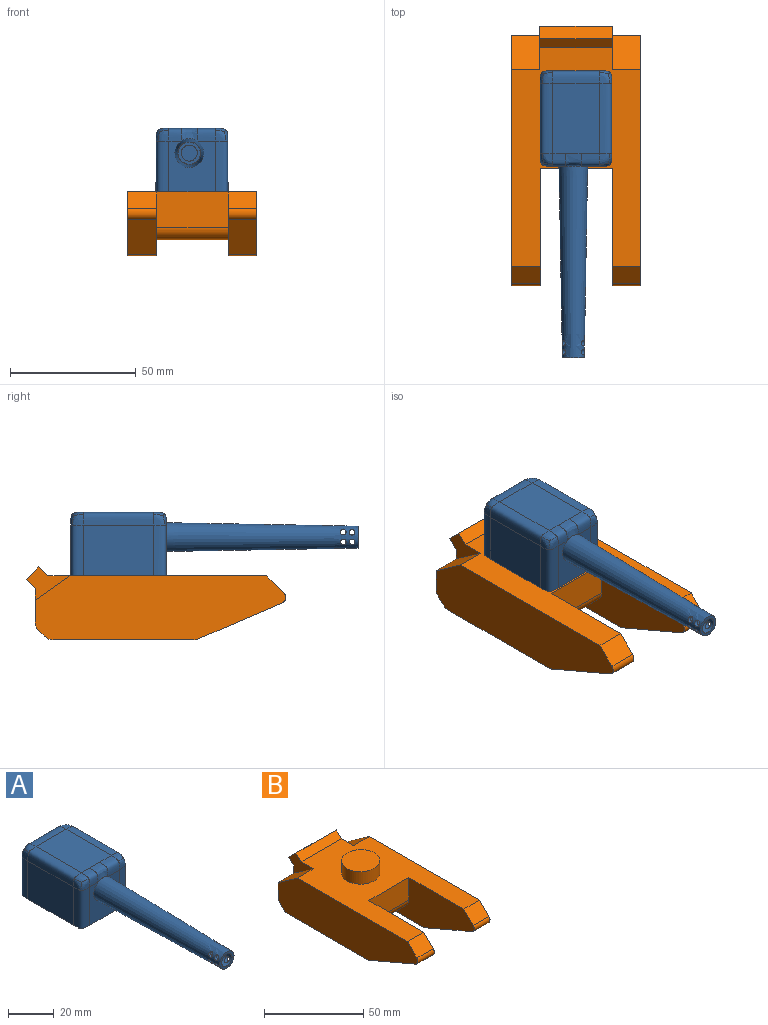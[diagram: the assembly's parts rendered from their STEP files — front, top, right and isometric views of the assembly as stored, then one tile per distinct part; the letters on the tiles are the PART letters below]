
ASSEMBLY  parts=2 mates=1
PART A: 42 faces, bbox 31.9x118.1x28.6 mm
  f0: cone r=5.71mm half-angle=1deg, axis (0,1,0), area 2380.8mm2, adj f4,f8,f25,f34,f35,f36,f37,f38
  f1: cone r=3.17mm half-angle=1deg, axis (0,1,0), area 1722.6mm2, adj f8,f33,f34,f35,f36,f37,f38,f39
  f2: plane 20.32x18.42mm, normal (0,1,0), area 374.2mm2, adj f7,f22,f26,f27
  f3: plane 27.94x20.32mm, normal (-1,0,0), area 567.7mm2, adj f7,f19,f21,f22
  f4: plane 20.32x18.42mm, normal (0,-1,0), area 275.4mm2, adj f0,f7,f19,f23,f28,f29
  f5: plane 27.94x20.32mm, normal (1,0,0), area 567.7mm2, adj f7,f27,f28,f32
  f6: plane 28.33x18.72mm, normal (0,0,1), area 514.8mm2, adj f21,f23,f25,f26,f29,f32
  f7: plane 39.99x30.47mm, normal (0,0,-1), area 764.9mm2, adj f2,f3,f4,f5,f9,f19,f22,f27
  f8: plane 8.77x8.77mm, normal (0,-1,0), area 28.7mm2, adj f0,f1
  f9: cylinder r=10.03mm len=20.07mm, axis (0,0,-1), area 485.2mm2, adj f7,f10
  f10: plane 20.07x20.07mm, normal (0,0,-1), area 316.2mm2, adj f9
  f11: bspline ~4.32x4.32mm, area 18.2mm2, adj f12,f28,f29,f31
  f12: bspline ~4.32x4.32mm, area 18.2mm2, adj f11,f28,f31,f32
  f13: bspline ~4.32x4.32mm, area 18.2mm2, adj f14,f26,f27,f30
  f14: bspline ~4.32x4.32mm, area 18.2mm2, adj f13,f26,f30,f32
  f15: bspline ~4.32x4.32mm, area 18.2mm2, adj f16,f21,f22,f24
  f16: bspline ~4.32x4.32mm, area 18.2mm2, adj f15,f21,f24,f26
  f17: bspline ~4.32x4.32mm, area 18.2mm2, adj f18,f19,f20,f21
  f18: bspline ~4.32x4.32mm, area 18.2mm2, adj f17,f19,f20,f23
  f19: bspline ~23.71x5.08mm, area 181.8mm2, adj f3,f4,f7,f17,f18
  f20: bspline ~4.32x4.32mm, area 18.2mm2, adj f17,f18,f21,f23
  f21: bspline ~37.25x5.08mm, area 250mm2, adj f3,f6,f15,f16,f17,f20
  f22: bspline ~23.71x5.08mm, area 181.8mm2, adj f2,f3,f7,f15,f24
  f23: bspline ~22.75x5.08mm, area 45.2mm2, adj f4,f6,f18,f20,f25
  f24: bspline ~4.32x4.32mm, area 18.2mm2, adj f15,f16,f22,f26
  f25: bspline ~6.18x5.08mm, area 50mm2, adj f0,f6,f23,f29
  f26: bspline ~27.09x5.08mm, area 164.8mm2, adj f2,f6,f13,f14,f16,f24
  f27: bspline ~23.71x5.08mm, area 181.8mm2, adj f2,f5,f7,f13,f30
  f28: bspline ~23.71x5.08mm, area 181.8mm2, adj f4,f5,f7,f11,f12
  f29: bspline ~27.09x5.08mm, area 64.3mm2, adj f4,f6,f11,f25,f31
  f30: bspline ~4.32x4.32mm, area 18.2mm2, adj f13,f14,f27,f32
  f31: bspline ~4.32x4.32mm, area 18.2mm2, adj f11,f12,f29,f32
  f32: bspline ~37.25x5.08mm, area 250mm2, adj f5,f6,f12,f14,f30,f31
  f33: plane 8.92x8.92mm, normal (0,-1,0), area 62.5mm2, adj f1
  f34: cylinder r=1.14mm len=3.39mm, axis (-1,0,0), area 10.1mm2, adj f0,f1
  f35: cylinder r=1.14mm len=3.5mm, axis (-1,0,0), area 11.3mm2, adj f0,f1
  f36: cylinder r=1.14mm len=3.32mm, axis (-1,0,0), area 10mm2, adj f0,f1
  f37: cylinder r=1.14mm len=3.43mm, axis (-1,0,0), area 11.2mm2, adj f0,f1
  f38: cylinder r=1.14mm len=3.33mm, axis (-1,0,0), area 11mm2, adj f0,f1
  f39: cylinder r=1.14mm len=3.34mm, axis (-1,0,0), area 11.2mm2, adj f0,f1
  f40: cylinder r=1.14mm len=3.39mm, axis (-1,0,0), area 11.1mm2, adj f0,f1
  f41: cylinder r=1.14mm len=3.39mm, axis (-1,0,0), area 11.2mm2, adj f0,f1
PART B: 33 faces, bbox 51.3x103.3x33 mm
  f0: plane 55.97x11.21mm, normal (0,0,-1), area 627.2mm2, adj f4,f16,f23,f29
  f1: plane 51.31x13.14mm, normal (0,1,0), area 570.5mm2, adj f3,f4,f5,f17,f18,f19,f20,f30
  f2: plane 33x14.12mm, normal (0,-0.39,-0.92), area 402.2mm2, adj f4,f13,f16,f23
  f3: plane 13.72x11.29mm, normal (0,0.58,0.82), area 189.5mm2, adj f1,f5,f7,f19
  f4: plane 99.69x25.4mm, normal (1,0,0), area 2153.6mm2, adj f0,f1,f2,f7,f11,f13,f16,f17
  f5: plane 99.69x25.4mm, normal (-1,0,0), area 2153.6mm2, adj f1,f3,f7,f8,f10,f12,f14,f15
  f6: plane 99.62x25.4mm, normal (1,0,0), area 1214.5mm2, adj f7,f8,f9,f10,f12,f14,f15,f24
  f7: plane 87.12x51.31mm, normal (0,0,1), area 2868.3mm2, adj f3,f4,f5,f6,f9,f10,f11,f17
  f8: plane 55.97x11.64mm, normal (0,0,-1), area 651.4mm2, adj f5,f6,f15,f28
  f9: plane 28.46x13.97mm, normal (0,-1,0), area 397.6mm2, adj f6,f7,f23,f25
  f10: plane 11.64x6.74mm, normal (0,-0.71,0.71), area 111mm2, adj f5,f6,f7,f14
  f11: plane 11.21x6.74mm, normal (0,-0.71,0.71), area 106.9mm2, adj f4,f7,f13,f23
  f12: plane 33x14.12mm, normal (0,-0.39,-0.92), area 417.7mm2, adj f5,f6,f14,f15
  f13: cylinder r=2.54mm len=11.21mm, axis (1,0,0), area 55.6mm2, adj f2,f4,f11,f23
  f14: cylinder r=2.54mm len=11.64mm, axis (1,0,0), area 57.7mm2, adj f5,f6,f10,f12
  f15: cylinder r=5.08mm len=11.64mm, axis (1,0,0), area 23.9mm2, adj f5,f6,f8,f12
  f16: cylinder r=5.08mm len=11.21mm, axis (1,0,0), area 23mm2, adj f0,f2,f4,f23
  f17: plane 13.72x11.29mm, normal (0,0.58,0.82), area 189.5mm2, adj f1,f4,f7,f18
  f18: plane 17.31x13.25mm, normal (1,0,0), area 89.9mm2, adj f1,f7,f17,f20,f21,f22
  f19: plane 17.31x13.25mm, normal (-1,0,0), area 89.9mm2, adj f1,f3,f7,f20,f21,f22
  f20: plane 28.72x3.59mm, normal (0,0.71,-0.71), area 145.9mm2, adj f1,f18,f19,f22
  f21: plane 28.72x3.59mm, normal (0,-0.71,0.71), area 145.9mm2, adj f7,f18,f19,f22
  f22: plane 28.72x5.08mm, normal (0,0.71,0.71), area 206.3mm2, adj f18,f19,f20,f21
  f23: plane 99.62x25.4mm, normal (-1,0,0), area 1214.5mm2, adj f0,f2,f7,f9,f11,f13,f16,f24
  f24: plane 47.92x28.46mm, normal (0,0,-1), area 1363.9mm2, adj f6,f23,f25,f30
  f25: cylinder r=5.08mm len=28.46mm, axis (-1,0,0), area 227.1mm2, adj f6,f9,f23,f24
  f26: plane 11.21x2.1mm, normal (0,0.71,-0.71), area 33.3mm2, adj f4,f23,f29,f30
  f27: plane 11.64x2.1mm, normal (0,0.71,-0.71), area 34.6mm2, adj f5,f6,f28,f30
  f28: cylinder r=5.08mm len=11.64mm, axis (1,0,0), area 46.4mm2, adj f5,f6,f8,f27
  f29: cylinder r=5.08mm len=11.21mm, axis (1,0,0), area 44.7mm2, adj f0,f4,f23,f26
  f30: cylinder r=5.08mm len=51.31mm, axis (-1,0,0), area 115mm2, adj f1,f4,f5,f6,f23,f24,f26,f27
  f31: cylinder r=9.65mm len=19.3mm, axis (0,0,-1), area 462.1mm2, adj f7,f32
  f32: plane 19.3x19.3mm, normal (0,0,1), area 292.7mm2, adj f31
PLACE A t=(-45.71,9.61,25.32)mm
PLACE B at identity
MATE cylindrical A.f9 <-> B.f31  axis (0,0,-1) through (0,17.58,33.02)mm
